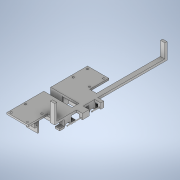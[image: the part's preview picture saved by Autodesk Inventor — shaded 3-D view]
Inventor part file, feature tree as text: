
AUTODESK INVENTOR PART (.ipt)
format: ipt  version: 2020.2 (Build 242310000, 310)  size: 749,056 bytes
history: native  units: mm
features: sketch x33, extrude x33, projected_geometry x12, hole x3
ambient origin geometry x8: Origin, YZ Plane, XZ Plane, XY Plane, X Axis, Y Axis, Z Axis, Center Point
bodies: Solid1 (feature_tree)
feature tree (81):
  sketch  "Sketch1"  dims[d0=8.0mm d1=98.298mm]
  extrude  "Extrusion1"  Depth=98.298mm
  extrude  "Extrusion2"  Depth=4.0mm
  extrude  "Extrusion3"  Depth=4.0mm TaperAngle=0.0deg
  extrude  "Extrusion4"  Depth=34.0mm
  extrude  "Extrusion5"  Depth=12.7mm
  extrude  "Extrusion6"  Depth=25.0mm
  hole  "Hole1"  [1 undecoded]
  extrude  "Extrusion11"  TaperAngle=60.0deg  [1 undecoded]
  extrude  "Extrusion12"  TaperAngle=120.0deg  [1 undecoded]
  sketch  "Sketch16"  dims[d19=6.4262mm d20=120.0deg]
  extrude  "Extrusion13"  Depth=6.4262mm
  extrude  "Extrusion14"  Depth=6.4262mm
  sketch  "Sketch17"  dims[d21=120.0deg d22=6.4262mm]
  extrude  "Extrusion15"  Depth=25.4mm TaperAngle=0.0deg
  extrude  "Extrusion18"  Depth=6.0mm
  extrude  "Extrusion19"  Depth=8.89mm
  extrude  "Extrusion20"  Depth=10.0mm
  hole  "Hole2"  [1 undecoded]
  extrude  "Extrusion21"  Depth=2.0mm
  extrude  "Extrusion22"  Depth=2.0mm
  sketch  "Sketch27"  dims[d45=8.89mm d46=2.0mm]
  extrude  "Extrusion23"  Depth=25.4mm
  extrude  "Extrusion24"  Depth=32.48mm
  extrude  "Extrusion25"  TaperAngle=90.0deg  [1 undecoded]
  sketch  "Sketch29"  dims[d79=51.53mm d80=32.48mm]
  extrude  "Extrusion26"  Depth=2.0mm
  extrude  "Extrusion27"  Depth=21.0mm
  extrude  "Extrusion28"  Depth=36.0mm TaperAngle=0.0deg
  extrude  "Extrusion29"  Depth=8.0mm
  extrude  "Extrusion30"  Depth=17.5mm
  extrude  "Extrusion32"  Depth=35.0mm
  extrude  "Extrusion33"  Depth=5.0mm
  extrude  "Extrusion34"  TaperAngle=90.0deg  [1 undecoded]
  extrude  "Extrusion35"  Depth=5.0mm
  extrude  "Extrusion38"  Depth=25.4mm TaperAngle=0.0deg
  extrude  "Extrusion39"  Depth=1.5mm
  extrude  "Extrusion40"  TaperAngle=0.0deg  [1 undecoded]
  hole  "Hole4"  [1 undecoded]
  extrude  "Extrusion43"  Depth=28.8036mm
  extrude  "Extrusion44"  Depth=25.4mm TaperAngle=0.0deg
  sketch  "Sketch2"  dims[d2=8.0mm d3=4.0mm]
  sketch  "Sketch3"  dims[d4=4.0mm d5=4.0mm d6=0.0mm]
  sketch  "Sketch4"  dims[d7=34.0mm d8=0.0mm d9=19.558mm]
  sketch  "Sketch5"  dims[d10=16.1125mm d11=12.7mm]
  sketch  "Sketch6"  dims[d12=25.0mm d13=0.0mm d14=11.1125mm]
  sketch  "Sketch14"  dims[d15=6.4135mm d16=12.827mm]
  projected_geometry  "Projected Loop2"
  sketch  "Sketch15"  dims[d17=6.4262mm d18=60.0deg]
  projected_geometry  "Projected Loop3"
  sketch  "Sketch18"  dims[d23=120.0deg d24=6.4262mm]
  sketch  "Sketch21"  dims[d25=120.0deg d26=25.4mm d27=0.0mm]
  sketch  "Sketch22"  dims[d28=6.0mm d29=8.89mm]
  sketch  "Sketch23"  dims[d30=5.9944mm d31=8.89mm]
  sketch  "Sketch24"  dims[d32=25.4mm d33=0.0mm d34=10.0mm]
  sketch  "Sketch25"  dims[d35=90.0deg d36=20.0mm]
  projected_geometry  "Projected Loop5"
  sketch  "Sketch26"  dims[d37=3.4mm d38=19.05mm d39=6.2992mm d40=6.35mm d41=90.0deg d42=5.0mm d43=0.0mm d44=2.0mm]
  sketch  "Sketch28"  dims[d47=25.4mm d48=0.0mm d78=16.24mm]
  sketch  "Sketch30"  dims[d81=90.0deg d82=90.0deg]
  sketch  "Sketch32"  dims[d83=4.0mm d84=0.0mm d87=2.0mm]
  projected_geometry  "Projected Loop6"
  sketch  "Sketch33"  dims[d88=2.0mm d89=21.0mm]
  projected_geometry  "Projected Loop7"
  sketch  "Sketch35"  dims[d90=2.0mm d91=36.0mm d92=0.0mm]
  projected_geometry  "Projected Loop8"
  sketch  "Sketch36"  dims[d93=13.878mm d94=8.0mm]
  sketch  "Sketch37"  dims[d95=180.0deg d96=17.5mm]
  sketch  "Sketch38"  dims[d97=90.0deg d98=35.0mm]
  sketch  "Sketch42"  dims[d99=3.5mm d100=5.0mm]
  sketch  "Sketch43"  dims[d101=7.0mm d102=90.0deg]
  projected_geometry  "Projected Loop9"
  projected_geometry  "Projected Loop10"
  projected_geometry  "Projected Loop11"
  projected_geometry  "Projected Loop12"
  sketch  "Sketch44"  dims[d103=5.0mm d104=3.4mm]
  sketch  "Sketch45"  dims[d105=3.4mm d106=25.4mm d107=0.0mm]
  sketch  "Sketch48"  dims[d108=6.4262mm d109=0.0mm d110=1.5mm]
  sketch  "Sketch49"  dims[d111=1.5mm d112=0.0mm d113=0.0mm d128=44.8mm d129=28.8036mm d130=25.4mm d131=0.0mm d132=3.2131mm d133=6.4262mm d134=120.0deg d135=3.2131mm d136=6.4262mm d137=120.0deg d138=25.4mm d139=0.0mm d140=8.001mm d141=13.8938mm d142=8.001mm d143=0.0mm d144=25.4mm d145=0.0mm d146=10.0mm d147=20.0mm d148=3.4mm d149=19.05mm d150=6.2992mm d151=6.35mm d152=90.0deg d153=5.0mm d154=0.0mm d155=16.2433mm d156=32.4866mm d157=51.5366mm d158=4.0mm d159=0.0mm d160=21.0mm d161=2.0mm d162=2.0mm d163=2.0mm d164=2.0mm d165=36.0mm d166=0.0mm d167=7.0mm d168=5.0mm d169=5.0mm d170=17.5mm d171=35.0mm d172=3.4mm d173=3.4mm d174=5.0mm d175=0.0mm d176=5.0mm d177=0.0mm d178=1.5mm d179=1.5mm d180=25.4mm d181=0.0mm d182=19.05mm d183=10.0mm d184=5.08mm d185=4.0mm d186=0.0mm d187=10.0mm d188=0.0mm d189=2.0mm d190=2.0mm d191=25.4mm d192=0.0mm d194=30.0mm d195=0.0mm d196=99.06mm d197=0.0mm d201=11.43mm d202=0.0mm d203=25.4mm d204=0.0mm d205=25.4mm d206=0.0mm d207=25.4mm d208=0.0mm d239=25.4mm d240=0.0mm d241=1.5mm d242=0.0mm d243=39.0mm d244=35.0mm d245=39.0mm d246=35.0mm d247=3.0mm d248=0.0mm d249=5.0mm d250=5.0mm d251=29.7mm d252=26.05mm d253=4.0mm d254=4.0mm d255=29.7mm d256=26.05mm d257=3.4mm d258=19.05mm d259=6.2992mm d260=6.35mm d261=90.0deg d262=25.4mm d263=20.594885mm d271=4.0mm d272=25.4mm d273=0.0mm d274=25.4mm d275=0.0mm d214=12.7mm d215=0.872665mm d216=12.7mm d217=0.872665mm d228=12.7mm d229=0.872665mm d230=12.7mm d231=0.872665mm]
  projected_geometry  "Projected Loop13"
  projected_geometry  "Projected Loop14"
note: 8 required parameter values undecoded (feature->parameter linkage not recoverable at this tier; creation-order binding heuristic only, values carry confidence <= 0.55)
